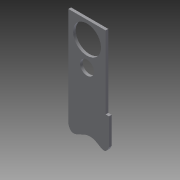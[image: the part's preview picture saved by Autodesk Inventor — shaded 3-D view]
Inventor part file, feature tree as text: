
AUTODESK INVENTOR PART (.ipt)
format: ipt  version: 2015 (Build 190159000, 159)  size: 93,696 bytes
history: native  units: mm
features: extrude x1, sketch x1
ambient origin geometry x8: Origin, YZ Plane, XZ Plane, XY Plane, X Axis, Y Axis, Z Axis, Center Point
bodies: Solid1 (feature_tree)
feature tree (2):
  extrude  "Extrusion1"  Depth=18.25mm
  sketch  "Sketch1"  dims[d0=10.5mm d2=18.25mm d3=21.0mm d4=14.0mm d5=13.0mm d6=28.0mm d7=54.75mm d8=2.5mm d9=20.25mm d10=62.0mm d11=2.0mm d12=0.0mm]
